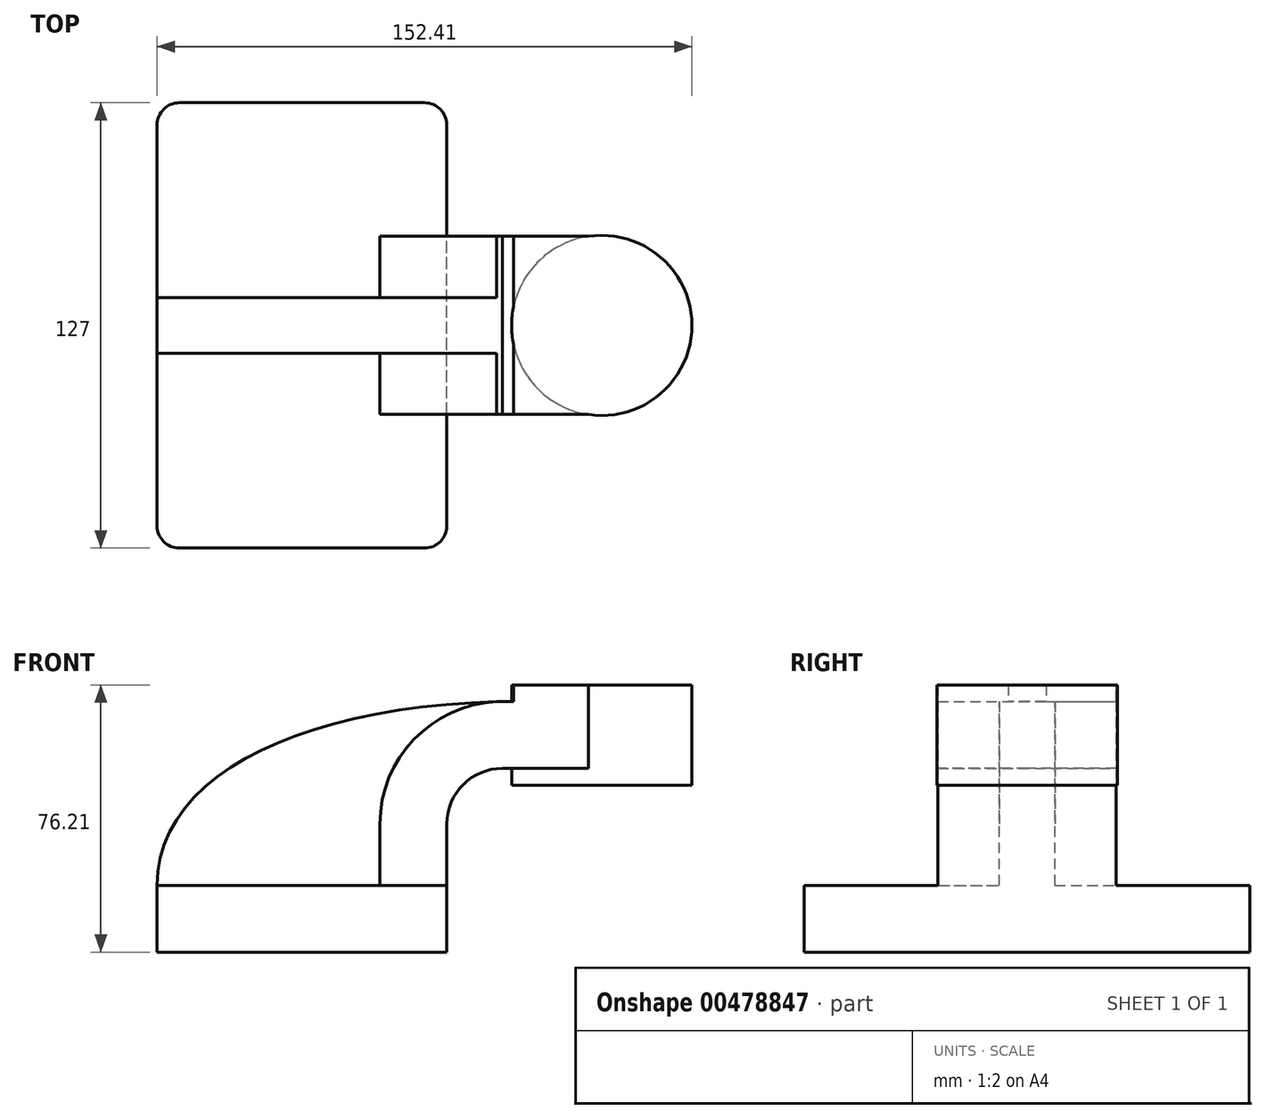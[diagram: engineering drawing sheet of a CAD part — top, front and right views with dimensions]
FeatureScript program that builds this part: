
annotation { "Feature Type Name" : "Feature", "Feature Type Description" : "" }
export const myFeature = defineFeature(function(context is Context, id is Id, definition is map)
    precondition{}
    {
        {
            var Q0;
            Q0=qCreatedBy(makeId("Front.planeOp"),FACE);
            var sketch = newSketch(context, id + "F0", { "sketchPlane" : qUnion([Q0])});
            skLineSegment(sketch, "E0.bottom", {"start": v(-41.28, 9.52) * mm, "end": v(41.28, 9.53) * mm});
            skLineSegment(sketch, "E0.top", {"start": v(-41.28, -9.53) * mm, "end": v(41.28, -9.53) * mm});
            skLineSegment(sketch, "E0.left", {"start": v(-41.28, 9.52) * mm, "end": v(-41.28, -9.53) * mm});
            skLineSegment(sketch, "E0.right", {"start": v(41.28, 9.53) * mm, "end": v(41.28, -9.52) * mm});
            skPoint(sketch, "E0.middle", {"position": v(0, 0) * mm});
            skLineSegment(sketch, "E1.bottom", {"start": v(60.32, 38.1) * mm, "end": v(111.12, 38.1) * mm});
            skLineSegment(sketch, "E1.top", {"start": v(60.32, 66.68) * mm, "end": v(111.12, 66.68) * mm});
            skLineSegment(sketch, "E1.left", {"start": v(60.32, 38.1) * mm, "end": v(60.32, 66.68) * mm});
            skLineSegment(sketch, "E1.right", {"start": v(111.12, 38.1) * mm, "end": v(111.12, 66.68) * mm});
            skPoint(sketch, "E1.middle", {"position": v(85.72, 52.39) * mm});
            skLineSegment(sketch, "E2", {"start": v(41.27, 9.53) * mm, "end": v(41.27, 27) * mm});
            skArc(sketch, "E3", {"start": v(41.27, 27) * mm, "mid": v(45.92, 38.23) * mm, "end": v(57.15, 42.88) * mm});
            skLineSegment(sketch, "E4", {"start": v(57.15, 42.88) * mm, "end": v(85.44, 42.88) * mm});
            skLineSegment(sketch, "E5.0", {"start": v(57.15, 61.93) * mm, "end": v(85.42, 61.93) * mm});
            skArc(sketch, "E5.1", {"start": v(22.22, 27) * mm, "mid": v(32.45, 51.7) * mm, "end": v(57.15, 61.93) * mm});
            skLineSegment(sketch, "E5.2", {"start": v(22.22, 9.53) * mm, "end": v(22.22, 27) * mm});
            skLineSegment(sketch, "E6", {"start": v(85.44, 38.1) * mm, "end": v(85.44, 66.68) * mm});
            skFitSpline(sketch, "E7", {"points": [v(-41.28, 9.52) * mm, v(57.15, 61.93) * mm], "startDerivative": vector(0.13, 94.66) * mm, "endDerivative": vector(171.45, 3.66) * mm});
            skSolve(sketch);
        }
        {
            var Q0;
            Q0=makeQuery(id+"F0.imprint","IMPRINT",FACE,{"disambiguationData":[TD([[makeQuery(id+"F0.imprint","IMPRINT",EDGE,{"derivedFrom":sQuery(id+"F0.wireOp",EDGE,"E0.top")}),1.0]])]});
            extrude(context, id + "F1", {"entities" : qUnion([Q0]), "endBound" : BoundingType.SYMMETRIC, "depth" : 127 * mm});
        }
        {
            var Q0;
            {var subQ3=sQuery(id+"F0.wireOp",EDGE,"E5.2");Q0=makeQuery(id+"F0.imprint","IMPRINT",FACE,{"disambiguationData":[TD([[makeQuery(id+"F0.imprint","IMPRINT",EDGE,{"derivedFrom":subQ3}),1.0]])]});}
            extrude(context, id + "F2", {"entities" : qUnion([Q0]), "operationType" : NewBodyOperationType.ADD, "endBound" : BoundingType.SYMMETRIC, "depth" : 15.88 * mm});
        }
        {
            var Q0;
            Q0=makeQuery(id+"F1.opExtrude","CAP_EDGE",EDGE,{"disambiguationData":[OSD([sQuery(id+"F0.wireOp",EDGE,"E0.right")])],"isStart":false});
            var Q1;
            Q1=makeQuery(id+"F1.opExtrude","CAP_EDGE",EDGE,{"disambiguationData":[OSD([sQuery(id+"F0.wireOp",EDGE,"E0.left")])],"isStart":false});
            var Q2;
            Q2=makeQuery(id+"F1.opExtrude","CAP_EDGE",EDGE,{"disambiguationData":[OSD([sQuery(id+"F0.wireOp",EDGE,"E0.right")])],"isStart":true});
            var Q3;
            Q3=makeQuery(id+"F1.opExtrude","CAP_EDGE",EDGE,{"disambiguationData":[OSD([sQuery(id+"F0.wireOp",EDGE,"E0.left")])],"isStart":true});
            fillet(context, id + "F3", {"entities" : qUnion([Q0, Q1, Q2, Q3]), "radius" : 6.35 * mm, "tangentPropagation" : true, "allowEdgeOverflow" : false});
        }
        {
            var Q0;
            {var subQ1=sQuery(id+"F0.wireOp",EDGE,"E2");Q0=makeQuery(id+"F0.imprint","IMPRINT",FACE,{"disambiguationData":[TD([[makeQuery(id+"F0.imprint","IMPRINT",EDGE,{"derivedFrom":subQ1}),1.0]])]});}
            var Q1;
            {var subQ3=sQuery(id+"F0.wireOp",EDGE,"E1.left");var subQ5=sQuery(id+"F0.wireOp",EDGE,"E1.top");var subQ6=makeQuery(id+"F0.imprint","INTERSECT",VERTEX,{"derivedFrom":[subQ5,subQ3]});Q1=makeQuery(id+"F0.imprint","IMPRINT",FACE,{"disambiguationData":[TD([[makeQuery(id+"F0.imprint","IMPRINT",EDGE,{"disambiguationData":[TD([[subQ6,-1.0]])],"derivedFrom":subQ5}),-1.0]])]});}
            extrude(context, id + "F4", {"entities" : qUnion([Q0, Q1]), "operationType" : NewBodyOperationType.ADD, "endBound" : BoundingType.SYMMETRIC, "depth" : 50.8 * mm});
        }
        {
            var Q0;
            {var subQ0=sQuery(id+"F0.wireOp",EDGE,"E1.right");Q0=makeQuery(id+"F0.imprint","IMPRINT",FACE,{"disambiguationData":[TD([[makeQuery(id+"F0.imprint","IMPRINT",EDGE,{"derivedFrom":subQ0}),1.0]])]});}
            var Q1;
            Q1=sQuery(id+"F0.wireOp",EDGE,"E6");
            revolve(context, id + "F5", {"operationType" : NewBodyOperationType.ADD, "entities" : qUnion([Q0]), "axis" : qUnion([Q1]), "revolveType" : RevolveType.FULL});
        }
    });
